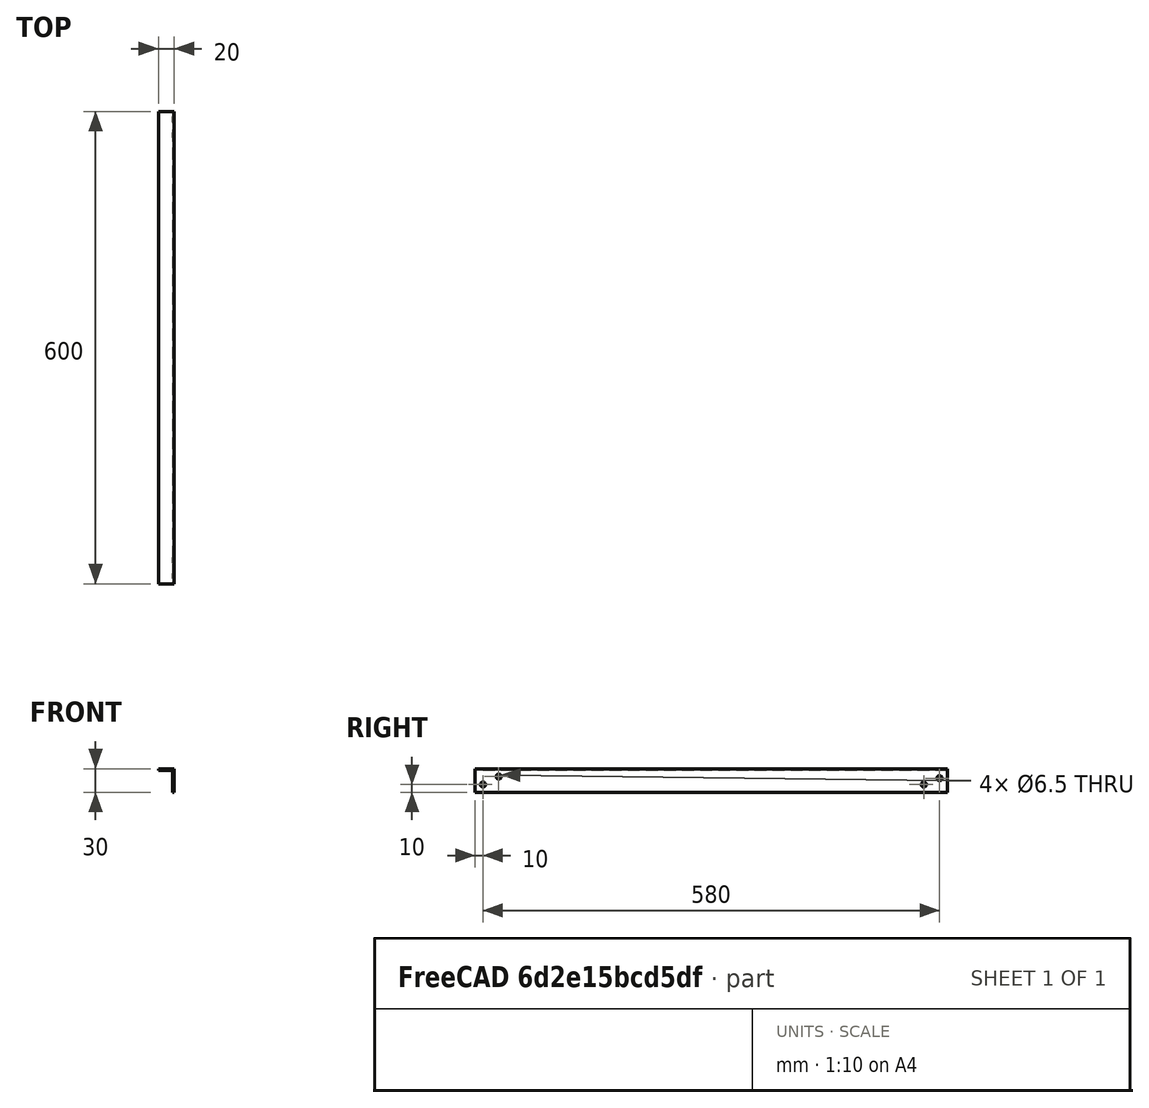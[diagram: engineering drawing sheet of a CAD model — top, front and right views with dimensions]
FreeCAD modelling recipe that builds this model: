
FCSTD DOCUMENT  (FreeCAD 0.18.4R)
Label: solar_panel_mount_bracket_2
License: All rights reserved
LicenseURL: http://en.wikipedia.org/wiki/All_rights_reserved
objects: TechDraw::DrawViewDimension×8, Sketcher::SketchObject×2, TechDraw::DrawProjGroupItem×2, PartDesign::Pad×1, PartDesign::Hole×1, PartDesign::Body×1, TechDraw::DrawSVGTemplate×1, TechDraw::DrawProjGroup×1, TechDraw::DrawPage×1
note: 7 computed .brp shape members not serialized (recipe doc carries the construction recipe); baked Part::Feature solids carry a one-line shape summary decoded from their .brp

FEATURE [Sketcher::SketchObject] Sketch
  MapMode = 5
  Placement = pos=(0,0,0) rot=(1,0,0;1.5708rad)
  Support = -> [XZ_Plane]
  sketch-geometry (6):
    g0: LineSegment StartX=-20 StartY=30 StartZ=0 EndX=0 EndY=30 EndZ=0
    g1: LineSegment StartX=0 StartY=30 StartZ=0 EndX=0 EndY=0 EndZ=0
    g2: LineSegment StartX=-20 StartY=30 StartZ=0 EndX=-20 EndY=28 EndZ=0
    g3: LineSegment StartX=-20 StartY=28 StartZ=0 EndX=-2 EndY=28 EndZ=0
    g4: LineSegment StartX=-2 StartY=28 StartZ=0 EndX=-2 EndY=0 EndZ=0
    g5: LineSegment StartX=-2 StartY=0 StartZ=0 EndX=0 EndY=0 EndZ=0
  constraints (17):
    c: Horizontal(g0)
    c: Coincident(g0,g1)
    c: Vertical(g1)
    c: DistanceX(g0,g0) = 20
    c: DistanceY(g1,g1) = 30
    c: Coincident(g1,g-1)
    c: Coincident(g2,g3)
    c: Horizontal(g3)
    c: Coincident(g3,g4)
    c: PointOnObject(g4,g-1)
    c: Vertical(g4)
    c: Coincident(g4,g5)
    c: Coincident(g5,g1)
    c: Parallel(g2,g1)
    c: Coincident(g2,g0)
    c: DistanceX(g5,g5) = 2
    c: DistanceY(g2,g2) = 2
FEATURE [PartDesign::Pad] Pad
  Length = 600
  Length2 = 100
  Placement = pos=(0,0,0) rot=(1,0,0;1.5708rad)
  Profile = -> Sketch
  Type = 0
FEATURE [Sketcher::SketchObject] Sketch001
  MapMode = 5
  Placement = pos=(-2,0,0) rot=(0.707107,0,-0.707107;3.14159rad)
  Support = -> [Pad]
  sketch-geometry (28):
    g0: LineSegment [constr] StartX=-28 StartY=40 StartZ=0 EndX=0 EndY=40 EndZ=0
    g1: LineSegment [constr] StartX=0 StartY=40 StartZ=0 EndX=0 EndY=0 EndZ=0
    g2: LineSegment [constr] StartX=0 StartY=0 StartZ=0 EndX=-28 EndY=0 EndZ=0
    g3: LineSegment [constr] StartX=-28 StartY=0 StartZ=0 EndX=-28 EndY=40 EndZ=0
    g4: LineSegment [constr] StartX=-28 StartY=10 StartZ=0 EndX=-18 EndY=10 EndZ=0
    g5: LineSegment [constr] StartX=-18 StartY=10 StartZ=0 EndX=-18 EndY=0 EndZ=0
    g6: LineSegment [constr] StartX=-18 StartY=0 StartZ=0 EndX=-28 EndY=0 EndZ=0
    g7: LineSegment [constr] StartX=-28 StartY=0 StartZ=0 EndX=-28 EndY=10 EndZ=0
    g8: Circle CenterX=-18 CenterY=10 CenterZ=0 NormalX=0 NormalY=0 NormalZ=1 AngleXU=0 Radius=3.25
    g9: LineSegment [constr] StartX=-10 StartY=40 StartZ=0 EndX=0 EndY=40 EndZ=0
    g10: LineSegment [constr] StartX=0 StartY=40 StartZ=0 EndX=0 EndY=30 EndZ=0
    g11: LineSegment [constr] StartX=0 StartY=30 StartZ=0 EndX=-10 EndY=30 EndZ=0
    g12: LineSegment [constr] StartX=-10 StartY=30 StartZ=0 EndX=-10 EndY=40 EndZ=0
    g13: Circle CenterX=-10 CenterY=30 CenterZ=0 NormalX=0 NormalY=0 NormalZ=1 AngleXU=0 Radius=3.25
    g14: LineSegment [constr] StartX=-28 StartY=600 StartZ=0 EndX=0 EndY=600 EndZ=0
    g15: LineSegment [constr] StartX=0 StartY=600 StartZ=0 EndX=0 EndY=560 EndZ=0
    g16: LineSegment [constr] StartX=0 StartY=560 StartZ=0 EndX=-28 EndY=560 EndZ=0
    g17: LineSegment [constr] StartX=-28 StartY=560 StartZ=0 EndX=-28 EndY=600 EndZ=0
    g18: LineSegment [constr] StartX=-28 StartY=570 StartZ=0 EndX=-20 EndY=570 EndZ=0
    g19: LineSegment [constr] StartX=-20 StartY=570 StartZ=0 EndX=-20 EndY=560 EndZ=0
    g20: LineSegment [constr] StartX=-20 StartY=560 StartZ=0 EndX=-28 EndY=560 EndZ=0
    g21: LineSegment [constr] StartX=-28 StartY=560 StartZ=0 EndX=-28 EndY=570 EndZ=0
    g22: LineSegment [constr] StartX=-10 StartY=590 StartZ=0 EndX=0 EndY=590 EndZ=0
    g23: LineSegment [constr] StartX=0 StartY=590 StartZ=0 EndX=0 EndY=600 EndZ=0
    g24: LineSegment [constr] StartX=0 StartY=600 StartZ=0 EndX=-10 EndY=600 EndZ=0
    g25: LineSegment [constr] StartX=-10 StartY=600 StartZ=0 EndX=-10 EndY=590 EndZ=0
    g26: Circle CenterX=-10 CenterY=590 CenterZ=0 NormalX=0 NormalY=0 NormalZ=1 AngleXU=0 Radius=3.25
    g27: Circle CenterX=-20 CenterY=570 CenterZ=0 NormalX=0 NormalY=0 NormalZ=1 AngleXU=0 Radius=3.25
  constraints (75):
    c: Coincident(g0,g1)
    c: Coincident(g1,g2)
    c: Coincident(g2,g3)
    c: Coincident(g3,g0)
    c: Horizontal(g0)
    c: Horizontal(g2)
    c: Vertical(g1)
    c: Vertical(g3)
    c: DistanceX(g2,g2) = 28
    c: Coincident(g1,g-1)
    c: DistanceY(g1,g1) = 40
    c: Coincident(g4,g5)
    c: Coincident(g5,g6)
    c: Coincident(g6,g7)
    c: Coincident(g7,g4)
    c: Horizontal(g4)
    c: Horizontal(g6)
    c: Vertical(g5)
    c: Vertical(g7)
    c: DistanceY(g5,g5) = 10
    c: DistanceX(g6,g6) = 10
    c: Coincident(g6,g2)
    c: Radius(g8) = 3.25
    c: Coincident(g8,g4)
    c: Coincident(g9,g10)
    c: Coincident(g10,g11)
    c: Coincident(g11,g12)
    c: Coincident(g12,g9)
    c: Horizontal(g9)
    c: Horizontal(g11)
    c: Vertical(g10)
    c: Vertical(g12)
    c: DistanceY(g10,g10) = 10
    c: DistanceX(g11,g11) = 10
    c: Coincident(g9,g0)
    c: Radius(g13) = 3.25
    c: Coincident(g13,g11)
    c: Coincident(g14,g15)
    c: Coincident(g15,g16)
    c: Coincident(g16,g17)
    c: Coincident(g17,g14)
    c: Horizontal(g14)
    c: Horizontal(g16)
    c: Vertical(g15)
    c: Vertical(g17)
    c: Coincident(g18,g19)
    c: Coincident(g19,g20)
    c: Coincident(g20,g21)
    c: Coincident(g21,g18)
    c: Horizontal(g18)
    c: Horizontal(g20)
    c: Vertical(g19)
    c: Vertical(g21)
    c: Coincident(g22,g23)
    c: Coincident(g23,g24)
    c: Coincident(g24,g25)
    c: Coincident(g25,g22)
    c: Horizontal(g22)
    c: Horizontal(g24)
    c: Vertical(g23)
    c: Vertical(g25)
    c: DistanceX(g20,g20) = 8
    c: DistanceY(g19,g19) = 10
    c: DistanceY(g17,g17) = 40
    c: DistanceX(g14,g14) = 28
    c: Coincident(g20,g16)
    c: DistanceX(g24,g24) = 10
    c: DistanceY(g23,g23) = 10
    c: Coincident(g23,g14)
    c: Radius(g26) = 3.25
    c: Radius(g27) = 3.25
    c: Coincident(g26,g22)
    c: Coincident(g27,g18)
    c: DistanceY(g-1,g15) = 560
    c: PointOnObject(g15,g-2)
FEATURE [PartDesign::Hole] Hole
  BaseFeature = -> Pad
  Depth = 25
  DepthType = 0
  Diameter = 6.5
  DrillPoint = 1
  DrillPointAngle = 118
  HoleCutCountersinkAngle = 90
  HoleCutDepth = 0
  HoleCutDiameter = 0
  HoleCutType = 0
  ModelActualThread = false
  Placement = pos=(0,0,0) rot=(1,0,0;1.5708rad)
  Profile = -> Sketch001
  Tapered = false
  TaperedAngle = 90
  ThreadAngle = 0
  ThreadClass = 0
  ThreadCutOffInner = 0
  ThreadCutOffOuter = 0
  ThreadDirection = 0
  ThreadFit = 0
  ThreadPitch = 0
  ThreadSize = 0
  ThreadType = 0
  Threaded = false
FEATURE [PartDesign::Body] Body
  Group = -> [Sketch,Pad,Sketch001,Hole]
  Origin = -> Origin
  Tip = -> Hole
FEATURE [TechDraw::DrawSVGTemplate] Template
  EditableTexts = AUTHOR_NAME=Norman Rembarz; DN=DN; DRAWING_TITLE=SensoLAB building instructions; FC-DATE=08/11/2020; FC-REV=REV A; FC-SC=1:1; FC-SH=1/1; FC-SI=A1; FreeCAD_DRAWING=mounting bracket No. 2; PN=PN; SI-4=for solar panel; SI-6=REGREEN PROJECT of EU
  Height = 594
  Orientation = 1
  Width = 841
FEATURE [TechDraw::DrawProjGroupItem] ProjItem  label="Front"
  CoarseView = false
  Direction = (-1,0,0)
  Focus = 100
  HardHidden = false
  IsoCount = 0
  IsoHidden = false
  IsoVisible = false
  LockPosition = true
  Perspective = false
  Rotation = 0
  RotationVector = (0,-1,0)
  ScaleType = 2
  SeamHidden = false
  SeamVisible = false
  SmoothHidden = false
  SmoothVisible = false
  Source = -> [Body]
  Type = 0
  X = 0
  Y = 0
FEATURE [TechDraw::DrawProjGroupItem] ProjItem001  label="Left"
  CoarseView = false
  Direction = (-1e-16,1,0)
  Focus = 100
  HardHidden = false
  IsoCount = 0
  IsoHidden = false
  IsoVisible = false
  LockPosition = false
  Perspective = false
  Rotation = 0
  RotationVector = (-1,-1e-16,0)
  ScaleType = 2
  SeamHidden = false
  SeamVisible = false
  SmoothHidden = false
  SmoothVisible = false
  Source = -> [Body]
  Type = 1
  X = 615
  Y = 0
FEATURE [TechDraw::DrawProjGroup] ProjGroup
  Anchor = -> ProjItem
  AutoDistribute = true
  LockPosition = false
  ProjectionType = 0
  Rotation = 0
  ScaleType = 0
  Source = -> [Body]
  Views = -> [ProjItem,ProjItem001]
  X = 401.502
  Y = 297
  spacingX = 15
  spacingY = 15
FEATURE [TechDraw::DrawViewDimension] Dimension
  Arbitrary = false
  FormatSpec = %.2f
  LockPosition = false
  MeasureType = 1
  OverTolerance = 0
  References2D = -> [ProjItem]
  Rotation = 0
  ScaleType = 0
  Type = 1
  UnderTolerance = 0
  X = 4.13564
  Y = 71.217
FEATURE [TechDraw::DrawViewDimension] Dimension001
  Arbitrary = false
  FormatSpec = %.2f
  LockPosition = false
  MeasureType = 1
  OverTolerance = 0
  References2D = -> [ProjItem]
  Rotation = 0
  ScaleType = 0
  Type = 2
  UnderTolerance = 0
  X = -340.438
  Y = -5.70988
FEATURE [TechDraw::DrawViewDimension] Dimension002
  Arbitrary = false
  FormatSpec = %.2f
  LockPosition = false
  MeasureType = 1
  OverTolerance = 0
  References2D = -> [ProjItem]
  Rotation = 0
  ScaleType = 0
  Type = 1
  UnderTolerance = 0
  X = -313.766
  Y = -30.2741
FEATURE [TechDraw::DrawViewDimension] Dimension003
  Arbitrary = false
  FormatSpec = %.2f
  LockPosition = false
  MeasureType = 1
  OverTolerance = 0
  References2D = -> [ProjItem]
  Rotation = 0
  ScaleType = 0
  Type = 1
  UnderTolerance = 0
  X = -286.492
  Y = -39.0927
FEATURE [TechDraw::DrawViewDimension] Dimension004
  Arbitrary = false
  FormatSpec = %.2f
  LockPosition = false
  MeasureType = 1
  OverTolerance = 0
  References2D = -> [ProjItem001]
  Rotation = 0
  ScaleType = 0
  Type = 1
  UnderTolerance = 0
  X = -21.1617
  Y = -17.581
FEATURE [TechDraw::DrawViewDimension] Dimension005
  Arbitrary = false
  FormatSpec = %.2f
  LockPosition = false
  MeasureType = 1
  OverTolerance = 0
  References2D = -> [ProjItem001]
  Rotation = 0
  ScaleType = 0
  Type = 1
  UnderTolerance = 0
  X = 0.933667
  Y = 37.2913
FEATURE [TechDraw::DrawViewDimension] Dimension006
  Arbitrary = false
  FormatSpec = %.2f
  LockPosition = false
  MeasureType = 1
  OverTolerance = 0
  References2D = -> [ProjItem001]
  Rotation = 0
  ScaleType = 0
  Type = 2
  UnderTolerance = 0
  X = 27.3467
  Y = 0.350125
FEATURE [TechDraw::DrawViewDimension] Dimension007
  Arbitrary = false
  FormatSpec = %.2f
  LockPosition = false
  MeasureType = 1
  OverTolerance = 0
  References2D = -> [ProjItem]
  Rotation = 0
  ScaleType = 0
  Type = 2
  UnderTolerance = 0
  X = -333.371
  Y = -27.9423
FEATURE [TechDraw::DrawPage] Page
  KeepUpdated = true
  ProjectionType = 0
  Template = -> Template
  Views = -> [ProjGroup,Dimension,Dimension001,Dimension002,Dimension003,Dimension004,Dimension005,Dimension006,Dimension007]
